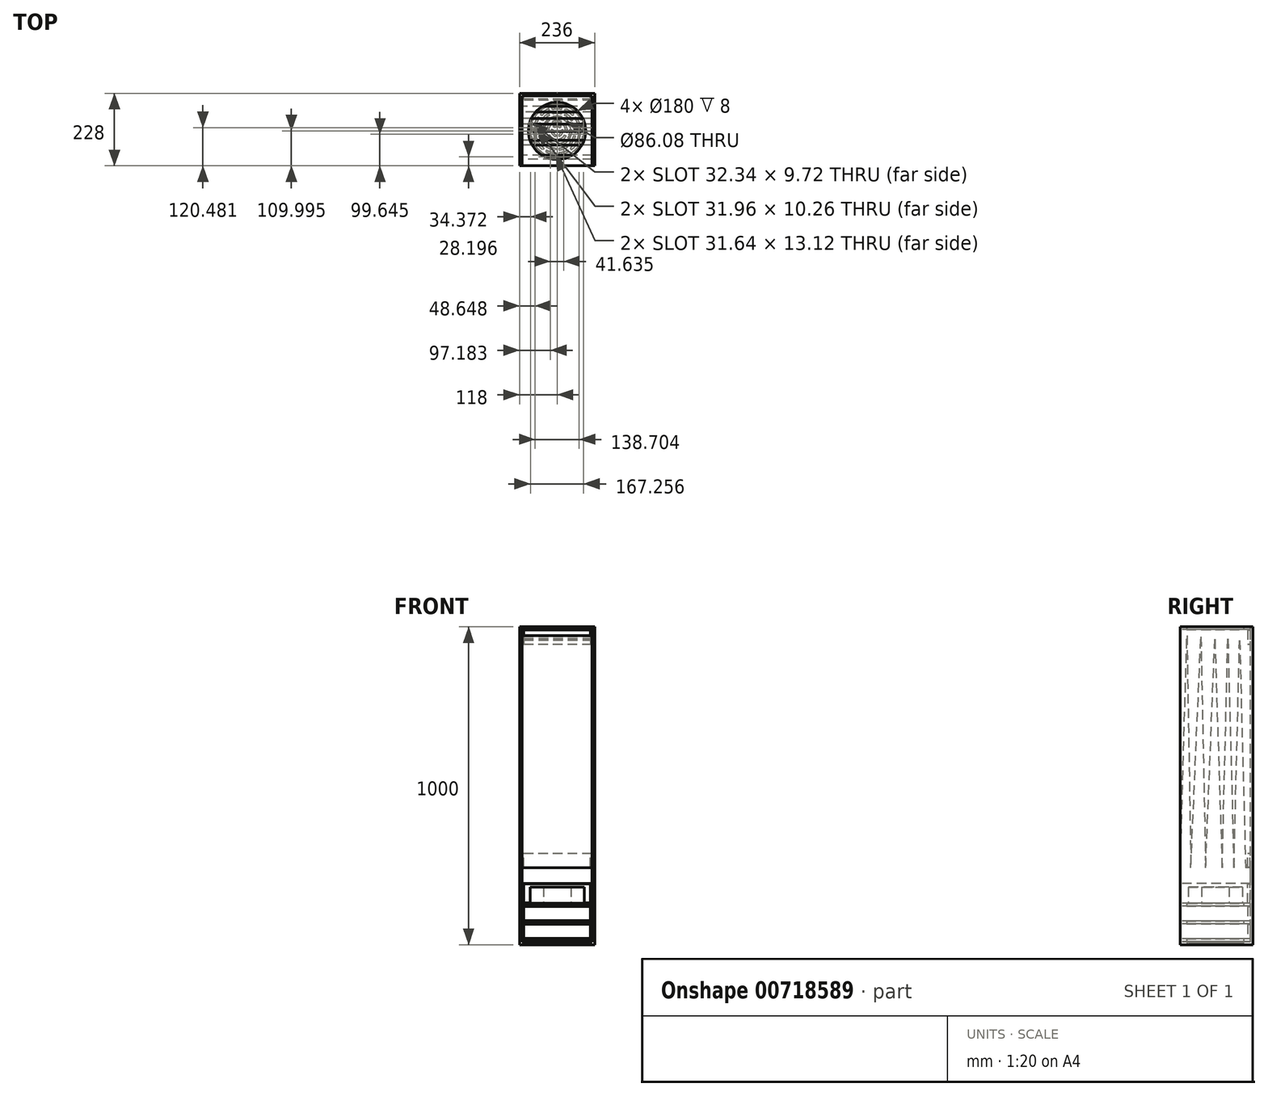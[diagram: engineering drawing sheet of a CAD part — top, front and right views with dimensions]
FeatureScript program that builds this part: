
annotation { "Feature Type Name" : "Feature", "Feature Type Description" : "" }
export const myFeature = defineFeature(function(context is Context, id is Id, definition is map)
    precondition{}
    {
        {
            var Q0;
            Q0=qCreatedBy(makeId("Top.planeOp"),FACE);
            var sketch = newSketch(context, id + "F0", { "sketchPlane" : qUnion([Q0])});
            skCircle(sketch, "E0", {"center": v(5.7, 12.26) * mm, "radius": 90 * mm});
            skLineSegment(sketch, "E1.bottom", {"start": v(-104.3, 122.26) * mm, "end": v(115.7, 122.26) * mm});
            skLineSegment(sketch, "E1.top", {"start": v(-104.3, -97.74) * mm, "end": v(115.7, -97.74) * mm});
            skLineSegment(sketch, "E1.left", {"start": v(-104.3, 122.26) * mm, "end": v(-104.3, -97.74) * mm});
            skLineSegment(sketch, "E1.right", {"start": v(115.7, 122.26) * mm, "end": v(115.7, -97.74) * mm});
            skSolve(sketch);
        }
        {
            var Q0;
            Q0=makeQuery(id+"F0.imprint","IMPRINT",FACE,{"disambiguationData":[TD([[makeQuery(id+"F0.imprint","IMPRINT",EDGE,{"derivedFrom":sQuery(id+"F0.wireOp",EDGE,"E0")}),-1.0]])]});
            extrude(context, id + "F1", {"entities" : qUnion([Q0]), "depth" : 8 * mm, "offsetDistance" : 25 * mm});
        }
        {
            var Q0;
            Q0=makeQuery(id+"F1.opExtrude","SWEPT_FACE",FACE,{"disambiguationData":[OSD([sQuery(id+"F0.wireOp",EDGE,"E1.left")])]});
            var sketch = newSketch(context, id + "F2", { "sketchPlane" : qUnion([Q0])});
            skLineSegment(sketch, "E2.bottom", {"start": v(-122.26, 8) * mm, "end": v(97.74, 8) * mm});
            skLineSegment(sketch, "E2.top", {"start": v(-122.26, -992) * mm, "end": v(97.74, -992) * mm});
            skLineSegment(sketch, "E2.left", {"start": v(-122.26, 8) * mm, "end": v(-122.26, -992) * mm});
            skLineSegment(sketch, "E2.right", {"start": v(97.74, 8) * mm, "end": v(97.74, -992) * mm});
            skSolve(sketch);
        }
        {
            var Q0;
            Q0 = qSketchRegion(id + "F2", true);
            extrude(context, id + "F3", {"entities" : qUnion([Q0]), "depth" : 8 * mm, "offsetDistance" : 25 * mm});
        }
        {
            var Q0;
            Q0=makeQuery(id+"F1.opExtrude","SWEPT_FACE",FACE,{"disambiguationData":[OSD([sQuery(id+"F0.wireOp",EDGE,"E1.bottom")])]});
            var sketch = newSketch(context, id + "F4", { "sketchPlane" : qUnion([Q0])});
            skLineSegment(sketch, "E3.bottom", {"start": v(-123.7, 8) * mm, "end": v(112.3, 8) * mm});
            skLineSegment(sketch, "E3.top", {"start": v(-123.7, -992) * mm, "end": v(112.3, -992) * mm});
            skLineSegment(sketch, "E3.left", {"start": v(-123.7, 8) * mm, "end": v(-123.7, -992) * mm});
            skLineSegment(sketch, "E3.right", {"start": v(112.3, 8) * mm, "end": v(112.3, -992) * mm});
            skSolve(sketch);
        }
        {
            var Q0;
            {var subQ1=sQuery(id+"F0.wireOp",EDGE,"E1.bottom");Q0=makeQuery(id+"F4.imprint","IMPRINT",FACE,{"disambiguationData":[TD([[makeQuery(id+"F4.imprint","IMPRINT",EDGE,{"derivedFrom":makeQuery(id+"F1.opExtrude","CAP_EDGE",EDGE,{"disambiguationData":[OSD([subQ1])],"isStart":true})}),-1.0]])]});}
            var Q1;
            Q1=makeQuery(id+"F4.imprint","IMPRINT",FACE,{"disambiguationData":[TD([[makeQuery(id+"F4.imprint","IMPRINT",EDGE,{"derivedFrom":sQuery(id+"F4.wireOp",EDGE,"E3.top")}),1.0]])]});
            extrude(context, id + "F5", {"entities" : qUnion([Q0, Q1]), "depth" : 8 * mm, "offsetDistance" : 25 * mm});
        }
        {
            var Q0;
            Q0=makeQuery(id+"F3.opExtrude","CAP_FACE",FACE,{"disambiguationData":[OSD([sQuery(id+"F2.wireOp",EDGE,"E2.bottom"),sQuery(id+"F2.wireOp",EDGE,"E2.top"),sQuery(id+"F2.wireOp",EDGE,"E2.left"),sQuery(id+"F2.wireOp",EDGE,"E2.right")])],"isStart":true});
            var sketch = newSketch(context, id + "F6", { "sketchPlane" : qUnion([Q0])});
            skLineSegment(sketch, "E4.top", {"start": v(122.26, -800) * mm, "end": v(-97.74, -800) * mm});
            skLineSegment(sketch, "E4.left", {"start": v(122.26, -750) * mm, "end": v(122.26, -800) * mm});
            skLineSegment(sketch, "E4.right", {"start": v(-97.74, -750) * mm, "end": v(-97.74, -800) * mm});
            skLineSegment(sketch, "E5", {"start": v(-97.74, -750) * mm, "end": v(-76.57, -19.39) * mm});
            skLineSegment(sketch, "E6", {"start": v(-76.57, -19.39) * mm, "end": v(-64.26, -750) * mm});
            skLineSegment(sketch, "E7", {"start": v(-64.26, -750) * mm, "end": v(-32.8, -23.5) * mm});
            skLineSegment(sketch, "E8", {"start": v(-32.8, -23.5) * mm, "end": v(-17.75, -750) * mm});
            skLineSegment(sketch, "E9", {"start": v(-17.75, -750) * mm, "end": v(10.98, -31.7) * mm});
            skLineSegment(sketch, "E10", {"start": v(10.98, -31.7) * mm, "end": v(34.23, -750) * mm});
            skLineSegment(sketch, "E11", {"start": v(34.23, -750) * mm, "end": v(52.02, -30.33) * mm});
            skLineSegment(sketch, "E12", {"start": v(52.02, -30.33) * mm, "end": v(71.17, -750) * mm});
            skLineSegment(sketch, "E13", {"start": v(71.17, -750) * mm, "end": v(88.95, -34.44) * mm});
            skLineSegment(sketch, "E14", {"start": v(88.95, -34.44) * mm, "end": v(108, -750) * mm});
            skLineSegment(sketch, "E15", {"start": v(122.26, -750) * mm, "end": v(108, -750) * mm});
            skSolve(sketch);
        }
        {
            var Q0;
            Q0 = qSketchRegion(id + "F6", true);
            extrude(context, id + "F7", {"entities" : qUnion([Q0]), "depth" : 220 * mm, "offsetDistance" : 25 * mm});
        }
        {
            var Q0;
            Q0=makeQuery(id+"F1.opExtrude","SWEPT_BODY",BODY,{"disambiguationData":[OSD([sQuery(id+"F0.wireOp",EDGE,"E0"),sQuery(id+"F0.wireOp",EDGE,"E1.bottom"),sQuery(id+"F0.wireOp",EDGE,"E1.top"),sQuery(id+"F0.wireOp",EDGE,"E1.left"),sQuery(id+"F0.wireOp",EDGE,"E1.right")])]});
            transform(context, id + "F8", {"entities" : qUnion([Q0]), "transformType" : TransformType.TRANSLATION_3D, "dx" : 0 * mm, "dy" : 0 * mm, "dz" : -870 * mm, "makeCopy" : true});
        }
        {
            var Q0;
            Q0=makeQuery(id+"F8.opPattern","COPY",BODY,{"derivedFrom":makeQuery(id+"F1.opExtrude","SWEPT_BODY",BODY,{"disambiguationData":[OSD([sQuery(id+"F0.wireOp",EDGE,"E0"),sQuery(id+"F0.wireOp",EDGE,"E1.bottom"),sQuery(id+"F0.wireOp",EDGE,"E1.top"),sQuery(id+"F0.wireOp",EDGE,"E1.left"),sQuery(id+"F0.wireOp",EDGE,"E1.right")])]}),"instanceName":"1"});
            transform(context, id + "F9", {"entities" : qUnion([Q0]), "transformType" : TransformType.TRANSLATION_3D, "dx" : 0 * mm, "dy" : 0 * mm, "dz" : -122 * mm, "makeCopy" : true});
        }
        {
            var Q0;
            Q0=makeQuery(id+"F8.opPattern","COPY",FACE,{"derivedFrom":makeQuery(id+"F1.opExtrude","CAP_FACE",FACE,{"disambiguationData":[OSD([sQuery(id+"F0.wireOp",EDGE,"E0"),sQuery(id+"F0.wireOp",EDGE,"E1.bottom"),sQuery(id+"F0.wireOp",EDGE,"E1.top"),sQuery(id+"F0.wireOp",EDGE,"E1.left"),sQuery(id+"F0.wireOp",EDGE,"E1.right")])],"isStart":false}),"instanceName":"1"});
            var sketch = newSketch(context, id + "F10", { "sketchPlane" : qUnion([Q0])});
            skCircle(sketch, "E16", {"center": v(5.7, 12.26) * mm, "radius": 85 * mm});
            skCircle(sketch, "E17", {"center": v(5.7, 12.26) * mm, "radius": 43.04 * mm});
            skSolve(sketch);
        }
        {
            var Q0;
            Q0=makeQuery(id+"F10.imprint","IMPRINT",FACE,{"disambiguationData":[TD([[makeQuery(id+"F10.imprint","IMPRINT",EDGE,{"derivedFrom":sQuery(id+"F10.wireOp",EDGE,"E16")}),1.0]])]});
            extrude(context, id + "F11", {"entities" : qUnion([Q0]), "depth" : 51 * mm, "offsetDistance" : 25 * mm});
        }
        {
            var Q0;
            Q0=makeQuery(id+"F9.opPattern","COPY",BODY,{"derivedFrom":makeQuery(id+"F8.opPattern","COPY",BODY,{"derivedFrom":makeQuery(id+"F1.opExtrude","SWEPT_BODY",BODY,{"disambiguationData":[OSD([sQuery(id+"F0.wireOp",EDGE,"E0"),sQuery(id+"F0.wireOp",EDGE,"E1.bottom"),sQuery(id+"F0.wireOp",EDGE,"E1.top"),sQuery(id+"F0.wireOp",EDGE,"E1.left"),sQuery(id+"F0.wireOp",EDGE,"E1.right")])]}),"instanceName":"1"}),"instanceName":"1"});
            transform(context, id + "F12", {"entities" : qUnion([Q0]), "transformType" : TransformType.TRANSLATION_3D, "dx" : 0 * mm, "dy" : 0 * mm, "dz" : 10 * mm, "makeCopy" : true});
        }
        {
            var Q0;
            Q0=makeQuery(id+"F12.opPattern","COPY",BODY,{"derivedFrom":makeQuery(id+"F9.opPattern","COPY",BODY,{"derivedFrom":makeQuery(id+"F8.opPattern","COPY",BODY,{"derivedFrom":makeQuery(id+"F1.opExtrude","SWEPT_BODY",BODY,{"disambiguationData":[OSD([sQuery(id+"F0.wireOp",EDGE,"E0"),sQuery(id+"F0.wireOp",EDGE,"E1.bottom"),sQuery(id+"F0.wireOp",EDGE,"E1.top"),sQuery(id+"F0.wireOp",EDGE,"E1.left"),sQuery(id+"F0.wireOp",EDGE,"E1.right")])]}),"instanceName":"1"}),"instanceName":"1"}),"instanceName":"1"});
            transform(context, id + "F13", {"entities" : qUnion([Q0]), "transformType" : TransformType.TRANSLATION_3D, "dx" : 0 * mm, "dy" : 0 * mm, "dz" : 56 * mm, "makeCopy" : true});
        }
        {
            var Q0;
            Q0=makeQuery(id+"F5.opExtrude","CAP_FACE",FACE,{"disambiguationData":[OSD([sQuery(id+"F4.wireOp",EDGE,"E3.bottom"),sQuery(id+"F4.wireOp",EDGE,"E3.top"),sQuery(id+"F4.wireOp",EDGE,"E3.left"),sQuery(id+"F4.wireOp",EDGE,"E3.right")])],"isStart":true});
            var sketch = newSketch(context, id + "F14", { "sketchPlane" : qUnion([Q0])});
            skLineSegment(sketch, "E18.bottom", {"start": v(-99.3, -928) * mm, "end": v(110.7, -928) * mm});
            skLineSegment(sketch, "E18.top", {"start": v(-99.3, -972) * mm, "end": v(110.7, -972) * mm});
            skLineSegment(sketch, "E18.left", {"start": v(-99.3, -928) * mm, "end": v(-99.3, -972) * mm});
            skLineSegment(sketch, "E18.right", {"start": v(110.7, -928) * mm, "end": v(110.7, -972) * mm});
            skLineSegment(sketch, "E19.bottom", {"start": v(-99.3, -872) * mm, "end": v(110.7, -872) * mm});
            skLineSegment(sketch, "E19.top", {"start": v(-99.3, -916) * mm, "end": v(110.7, -916) * mm});
            skLineSegment(sketch, "E19.left", {"start": v(-99.3, -872) * mm, "end": v(-99.3, -916) * mm});
            skLineSegment(sketch, "E19.right", {"start": v(110.7, -872) * mm, "end": v(110.7, -916) * mm});
            skLineSegment(sketch, "E20.bottom", {"start": v(-99.3, -860) * mm, "end": v(110.7, -860) * mm});
            skLineSegment(sketch, "E20.top", {"start": v(-99.3, -801) * mm, "end": v(110.7, -801) * mm});
            skLineSegment(sketch, "E20.left", {"start": v(-99.3, -860) * mm, "end": v(-99.3, -801) * mm});
            skLineSegment(sketch, "E20.right", {"start": v(110.7, -860) * mm, "end": v(110.7, -801) * mm});
            skLineSegment(sketch, "E21.bottom", {"start": v(-99.3, -748) * mm, "end": v(110.7, -748) * mm});
            skLineSegment(sketch, "E21.top", {"start": v(-99.3, -704) * mm, "end": v(110.7, -704) * mm});
            skLineSegment(sketch, "E21.left", {"start": v(-99.3, -748) * mm, "end": v(-99.3, -704) * mm});
            skLineSegment(sketch, "E21.right", {"start": v(110.7, -748) * mm, "end": v(110.7, -704) * mm});
            skLineSegment(sketch, "E22.bottom", {"start": v(-99.3, -2) * mm, "end": v(110.7, -2) * mm});
            skLineSegment(sketch, "E22.top", {"start": v(-99.3, -46) * mm, "end": v(110.7, -46) * mm});
            skLineSegment(sketch, "E22.left", {"start": v(-99.3, -2) * mm, "end": v(-99.3, -46) * mm});
            skLineSegment(sketch, "E22.right", {"start": v(110.7, -2) * mm, "end": v(110.7, -46) * mm});
            skSolve(sketch);
        }
        {
            var Q0;
            Q0 = qSketchRegion(id + "F14", true);
            extrude(context, id + "F15", {"entities" : qUnion([Q0]), "depth" : 8 * mm, "offsetDistance" : 25 * mm});
        }
        {
            var Q0;
            Q0=makeQuery(id+"F3.opExtrude","SWEPT_BODY",BODY,{"disambiguationData":[OSD([sQuery(id+"F2.wireOp",EDGE,"E2.bottom"),sQuery(id+"F2.wireOp",EDGE,"E2.top"),sQuery(id+"F2.wireOp",EDGE,"E2.left"),sQuery(id+"F2.wireOp",EDGE,"E2.right")])]});
            transform(context, id + "F16", {"entities" : qUnion([Q0]), "transformType" : TransformType.TRANSLATION_3D, "dx" : 228 * mm, "dy" : 0 * mm, "dz" : 0 * mm, "makeCopy" : true});
        }
        {
            var Q0;
            Q0=makeQuery(id+"F9.opPattern","COPY",FACE,{"derivedFrom":makeQuery(id+"F8.opPattern","COPY",FACE,{"derivedFrom":makeQuery(id+"F1.opExtrude","CAP_FACE",FACE,{"disambiguationData":[OSD([sQuery(id+"F0.wireOp",EDGE,"E0"),sQuery(id+"F0.wireOp",EDGE,"E1.bottom"),sQuery(id+"F0.wireOp",EDGE,"E1.top"),sQuery(id+"F0.wireOp",EDGE,"E1.left"),sQuery(id+"F0.wireOp",EDGE,"E1.right")])],"isStart":true}),"instanceName":"1"}),"instanceName":"1"});
            var sketch = newSketch(context, id + "F17", { "sketchPlane" : qUnion([Q0])});
            skArc(sketch, "E23", {"start": v(18.11, -13.65) * mm, "mid": v(16.52, -6) * mm, "end": v(10.7, -0.8) * mm});
            skArc(sketch, "E24", {"start": v(23.62, -16.83) * mm, "mid": v(21.71, -3) * mm, "end": v(10.7, 5.56) * mm});
            skArc(sketch, "E25.0", {"start": v(-20.6, -8.97) * mm, "mid": v(-19.51, -20.44) * mm, "end": v(-13.65, -30.37) * mm});
            skArc(sketch, "E26.0", {"start": v(-26.4, -7.09) * mm, "mid": v(-25.22, -22.3) * mm, "end": v(-17.23, -35.3) * mm});
            skArc(sketch, "E27.0", {"start": v(-28.85, 8.9) * mm, "mid": v(-33.8, -3.24) * mm, "end": v(-34.6, -16.32) * mm});
            skArc(sketch, "E28.0", {"start": v(-33.57, 12.66) * mm, "mid": v(-39.64, -1.9) * mm, "end": v(-40.5, -17.67) * mm});
            skArc(sketch, "E29.0", {"start": v(-48.62, -7.76) * mm, "mid": v(-47.98, -21.72) * mm, "end": v(-43.8, -35.06) * mm});
            skArc(sketch, "E30.0", {"start": v(-54.56, -6.7) * mm, "mid": v(-53.9, -22.76) * mm, "end": v(-49.03, -38.07) * mm});
            skArc(sketch, "E31.0", {"start": v(-8.76, -79.21) * mm, "mid": v(5.7, -80.76) * mm, "end": v(20.14, -79.21) * mm});
            skArc(sketch, "E32.0", {"start": v(-10.45, -84.99) * mm, "mid": v(5.7, -86.76) * mm, "end": v(21.83, -84.99) * mm});
            skArc(sketch, "E33.0", {"start": v(-9.16, -93.4) * mm, "mid": v(5.7, -94.76) * mm, "end": v(20.54, -93.4) * mm});
            skArc(sketch, "E34.0", {"start": v(-10.6, -99.24) * mm, "mid": v(5.7, -100.76) * mm, "end": v(21.98, -99.24) * mm});
            skLineSegment(sketch, "E35.0", {"start": v(0.7, -0.8) * mm, "end": v(0.7, 5.56) * mm});
            skLineSegment(sketch, "E36.0", {"start": v(10.7, -0.8) * mm, "end": v(10.7, 5.56) * mm});
            skLineSegment(sketch, "E37.trimOffspring", {"start": v(0.7, 13.77) * mm, "end": v(0.7, 19.86) * mm});
            skLineSegment(sketch, "E38.trimOffspring", {"start": v(10.7, 13.77) * mm, "end": v(10.7, 19.86) * mm});
            skLineSegment(sketch, "E39.trimOffspring", {"start": v(10.7, 27.93) * mm, "end": v(10.7, 33.97) * mm});
            skLineSegment(sketch, "E40.trimOffspring", {"start": v(0.7, 27.93) * mm, "end": v(0.7, 33.97) * mm});
            skLineSegment(sketch, "E41.trimOffspring", {"start": v(10.7, 42.01) * mm, "end": v(10.7, 48.04) * mm});
            skLineSegment(sketch, "E42.trimOffspring", {"start": v(0.7, 42.01) * mm, "end": v(0.7, 48.04) * mm});
            skLineSegment(sketch, "E43.trimOffspring", {"start": v(0.7, 56.06) * mm, "end": v(0.7, 62.08) * mm});
            skLineSegment(sketch, "E44.trimOffspring", {"start": v(10.7, 56.06) * mm, "end": v(10.7, 62.08) * mm});
            skLineSegment(sketch, "E45.trimOffspring", {"start": v(10.7, 70.1) * mm, "end": v(10.7, 76.1) * mm});
            skLineSegment(sketch, "E46.trimOffspring", {"start": v(0.7, 70.1) * mm, "end": v(0.7, 76.1) * mm});
            skLineSegment(sketch, "E47.1.0", {"start": v(-6.73, -13.65) * mm, "end": v(-12.24, -16.83) * mm});
            skLineSegment(sketch, "E47.1.1", {"start": v(-1.73, -22.31) * mm, "end": v(-7.24, -25.5) * mm});
            skLineSegment(sketch, "E47.2.0", {"start": v(13.11, -22.31) * mm, "end": v(18.62, -25.5) * mm});
            skLineSegment(sketch, "E47.2.1", {"start": v(18.11, -13.65) * mm, "end": v(23.62, -16.83) * mm});
            skLineSegment(sketch, "E48.1.0", {"start": v(-17.52, 0.54) * mm, "end": v(-23.3, 2.42) * mm});
            skLineSegment(sketch, "E48.1.1", {"start": v(-20.6, -8.97) * mm, "end": v(-26.4, -7.09) * mm});
            skLineSegment(sketch, "E48.2.0", {"start": v(-13.65, -30.37) * mm, "end": v(-17.23, -35.3) * mm});
            skLineSegment(sketch, "E48.2.1", {"start": v(-5.56, -36.25) * mm, "end": v(-9.14, -41.17) * mm});
            skLineSegment(sketch, "E48.3.0", {"start": v(16.94, -36.25) * mm, "end": v(20.52, -41.17) * mm});
            skLineSegment(sketch, "E48.3.1", {"start": v(25.03, -30.37) * mm, "end": v(28.61, -35.3) * mm});
            skLineSegment(sketch, "E48.4.0", {"start": v(31.99, -8.97) * mm, "end": v(37.78, -7.09) * mm});
            skLineSegment(sketch, "E48.4.1", {"start": v(28.9, 0.54) * mm, "end": v(34.69, 2.42) * mm});
            skLineSegment(sketch, "E49.1.0", {"start": v(-22.61, 16.71) * mm, "end": v(-27.34, 20.48) * mm});
            skLineSegment(sketch, "E49.1.1", {"start": v(-28.85, 8.9) * mm, "end": v(-33.57, 12.66) * mm});
            skLineSegment(sketch, "E49.2.0", {"start": v(-34.6, -16.32) * mm, "end": v(-40.5, -17.67) * mm});
            skLineSegment(sketch, "E49.2.1", {"start": v(-32.38, -26.07) * mm, "end": v(-38.27, -27.42) * mm});
            skLineSegment(sketch, "E49.3.0", {"start": v(-16.25, -46.3) * mm, "end": v(-18.87, -51.74) * mm});
            skLineSegment(sketch, "E49.3.1", {"start": v(-7.24, -50.63) * mm, "end": v(-9.86, -56.08) * mm});
            skLineSegment(sketch, "E49.4.0", {"start": v(18.62, -50.63) * mm, "end": v(21.24, -56.08) * mm});
            skLineSegment(sketch, "E49.4.1", {"start": v(27.63, -46.3) * mm, "end": v(30.25, -51.74) * mm});
            skLineSegment(sketch, "E49.5.0", {"start": v(43.76, -26.07) * mm, "end": v(49.65, -27.42) * mm});
            skLineSegment(sketch, "E49.5.1", {"start": v(45.99, -16.32) * mm, "end": v(51.87, -17.67) * mm});
            skLineSegment(sketch, "E49.6.0", {"start": v(40.23, 8.9) * mm, "end": v(44.95, 12.66) * mm});
            skLineSegment(sketch, "E49.6.1", {"start": v(34, 16.71) * mm, "end": v(38.72, 20.48) * mm});
            skLineSegment(sketch, "E50.1.0", {"start": v(-25.36, 32.53) * mm, "end": v(-29.24, 37.15) * mm});
            skLineSegment(sketch, "E50.1.1", {"start": v(-33.02, 26.1) * mm, "end": v(-36.9, 30.72) * mm});
            skLineSegment(sketch, "E50.2.0", {"start": v(-46.89, 2.1) * mm, "end": v(-52.82, 3.14) * mm});
            skLineSegment(sketch, "E50.2.1", {"start": v(-48.62, -7.76) * mm, "end": v(-54.56, -6.7) * mm});
            skLineSegment(sketch, "E50.3.0", {"start": v(-43.8, -35.06) * mm, "end": v(-49.03, -38.07) * mm});
            skLineSegment(sketch, "E50.3.1", {"start": v(-38.8, -43.72) * mm, "end": v(-44.03, -46.73) * mm});
            skLineSegment(sketch, "E50.4.0", {"start": v(-17.57, -61.54) * mm, "end": v(-19.63, -67.2) * mm});
            skLineSegment(sketch, "E50.4.1", {"start": v(-8.17, -64.96) * mm, "end": v(-10.23, -70.62) * mm});
            skLineSegment(sketch, "E50.5.0", {"start": v(19.55, -64.96) * mm, "end": v(21.61, -70.62) * mm});
            skLineSegment(sketch, "E50.5.1", {"start": v(28.95, -61.54) * mm, "end": v(31.01, -67.2) * mm});
            skLineSegment(sketch, "E50.6.0", {"start": v(50.19, -43.72) * mm, "end": v(55.4, -46.73) * mm});
            skLineSegment(sketch, "E50.6.1", {"start": v(55.19, -35.06) * mm, "end": v(60.4, -38.07) * mm});
            skLineSegment(sketch, "E50.7.0", {"start": v(60, -7.76) * mm, "end": v(65.94, -6.7) * mm});
            skLineSegment(sketch, "E50.7.1", {"start": v(58.27, 2.1) * mm, "end": v(64.2, 3.14) * mm});
            skLineSegment(sketch, "E50.8.0", {"start": v(44.4, 26.1) * mm, "end": v(48.28, 30.72) * mm});
            skLineSegment(sketch, "E50.8.1", {"start": v(36.74, 32.53) * mm, "end": v(40.62, 37.15) * mm});
            skLineSegment(sketch, "E51.1.0", {"start": v(-27.04, 47.92) * mm, "end": v(-30.3, 52.98) * mm});
            skLineSegment(sketch, "E51.1.1", {"start": v(-35.45, 42.51) * mm, "end": v(-38.7, 47.57) * mm});
            skLineSegment(sketch, "E51.2.0", {"start": v(-54.38, 20.67) * mm, "end": v(-59.85, 23.17) * mm});
            skLineSegment(sketch, "E51.2.1", {"start": v(-58.53, 11.58) * mm, "end": v(-64, 14.08) * mm});
            skLineSegment(sketch, "E51.3.0", {"start": v(-62.64, -17.03) * mm, "end": v(-68.6, -17.88) * mm});
            skLineSegment(sketch, "E51.3.1", {"start": v(-61.22, -26.93) * mm, "end": v(-67.17, -27.78) * mm});
            skLineSegment(sketch, "E51.4.0", {"start": v(-49.21, -53.22) * mm, "end": v(-53.76, -57.15) * mm});
            skLineSegment(sketch, "E51.4.1", {"start": v(-42.67, -60.77) * mm, "end": v(-47.21, -64.71) * mm});
            skLineSegment(sketch, "E51.5.0", {"start": v(-18.35, -76.4) * mm, "end": v(-20.05, -82.17) * mm});
            skLineSegment(sketch, "E51.5.1", {"start": v(-8.76, -79.21) * mm, "end": v(-10.45, -84.99) * mm});
            skLineSegment(sketch, "E51.6.0", {"start": v(20.14, -79.21) * mm, "end": v(21.83, -84.99) * mm});
            skLineSegment(sketch, "E51.6.1", {"start": v(29.73, -76.4) * mm, "end": v(31.43, -82.17) * mm});
            skLineSegment(sketch, "E51.7.0", {"start": v(54.05, -60.77) * mm, "end": v(58.6, -64.71) * mm});
            skLineSegment(sketch, "E51.7.1", {"start": v(60.6, -53.22) * mm, "end": v(65.14, -57.15) * mm});
            skLineSegment(sketch, "E51.8.0", {"start": v(72.6, -26.93) * mm, "end": v(78.55, -27.78) * mm});
            skLineSegment(sketch, "E51.8.1", {"start": v(74.02, -17.03) * mm, "end": v(79.98, -17.88) * mm});
            skLineSegment(sketch, "E51.9.0", {"start": v(69.91, 11.58) * mm, "end": v(75.38, 14.08) * mm});
            skLineSegment(sketch, "E51.9.1", {"start": v(65.76, 20.67) * mm, "end": v(71.23, 23.17) * mm});
            skLineSegment(sketch, "E51.10.0", {"start": v(46.83, 42.51) * mm, "end": v(50.08, 47.57) * mm});
            skLineSegment(sketch, "E51.10.1", {"start": v(38.42, 47.92) * mm, "end": v(41.67, 52.98) * mm});
            skLineSegment(sketch, "E52.1.0", {"start": v(-28.15, 62.98) * mm, "end": v(-30.94, 68.3) * mm});
            skLineSegment(sketch, "E52.1.1", {"start": v(-37, 58.34) * mm, "end": v(-39.8, 63.66) * mm});
            skLineSegment(sketch, "E52.2.0", {"start": v(-59.24, 38.64) * mm, "end": v(-64.19, 42.05) * mm});
            skLineSegment(sketch, "E52.2.1", {"start": v(-64.92, 30.4) * mm, "end": v(-69.87, 33.82) * mm});
            skLineSegment(sketch, "E52.3.0", {"start": v(-75.46, 2.63) * mm, "end": v(-81.42, 3.36) * mm});
            skLineSegment(sketch, "E52.3.1", {"start": v(-76.66, -7.3) * mm, "end": v(-82.63, -6.57) * mm});
            skLineSegment(sketch, "E52.4.0", {"start": v(-73.08, -36.78) * mm, "end": v(-78.7, -38.91) * mm});
            skLineSegment(sketch, "E52.4.1", {"start": v(-69.53, -46.13) * mm, "end": v(-75.15, -48.26) * mm});
            skLineSegment(sketch, "E52.5.0", {"start": v(-52.66, -70.58) * mm, "end": v(-56.64, -75.08) * mm});
            skLineSegment(sketch, "E52.5.1", {"start": v(-45.17, -77.2) * mm, "end": v(-49.16, -81.7) * mm});
            skLineSegment(sketch, "E52.6.0", {"start": v(-18.87, -91.01) * mm, "end": v(-20.31, -96.85) * mm});
            skLineSegment(sketch, "E52.6.1", {"start": v(-9.16, -93.4) * mm, "end": v(-10.6, -99.24) * mm});
            skLineSegment(sketch, "E52.7.0", {"start": v(20.54, -93.4) * mm, "end": v(21.98, -99.24) * mm});
            skLineSegment(sketch, "E52.7.1", {"start": v(30.25, -91.01) * mm, "end": v(31.7, -96.85) * mm});
            skLineSegment(sketch, "E52.8.0", {"start": v(56.55, -77.2) * mm, "end": v(60.54, -81.7) * mm});
            skLineSegment(sketch, "E52.8.1", {"start": v(64.04, -70.58) * mm, "end": v(68.03, -75.08) * mm});
            skLineSegment(sketch, "E52.9.0", {"start": v(80.91, -46.13) * mm, "end": v(86.53, -48.26) * mm});
            skLineSegment(sketch, "E52.9.1", {"start": v(84.46, -36.78) * mm, "end": v(90.08, -38.91) * mm});
            skLineSegment(sketch, "E52.10.0", {"start": v(88.04, -7.3) * mm, "end": v(94, -6.57) * mm});
            skLineSegment(sketch, "E52.10.1", {"start": v(86.84, 2.63) * mm, "end": v(92.8, 3.36) * mm});
            skLineSegment(sketch, "E52.11.0", {"start": v(76.3, 30.4) * mm, "end": v(81.25, 33.82) * mm});
            skLineSegment(sketch, "E52.11.1", {"start": v(70.62, 38.64) * mm, "end": v(75.57, 42.05) * mm});
            skLineSegment(sketch, "E52.12.0", {"start": v(48.39, 58.34) * mm, "end": v(51.18, 63.66) * mm});
            skLineSegment(sketch, "E52.12.1", {"start": v(39.53, 62.98) * mm, "end": v(42.33, 68.3) * mm});
            skArc(sketch, "E53.trimOffspring", {"start": v(0.7, -0.8) * mm, "mid": v(-5.14, -6) * mm, "end": v(-6.73, -13.65) * mm});
            skArc(sketch, "E54.trimOffspring", {"start": v(0.7, 5.56) * mm, "mid": v(-10.33, -3) * mm, "end": v(-12.24, -16.83) * mm});
            skArc(sketch, "E55.trimOffspring", {"start": v(-1.73, -22.31) * mm, "mid": v(5.7, -24.76) * mm, "end": v(13.11, -22.31) * mm});
            skArc(sketch, "E56.trimOffspring", {"start": v(-7.24, -25.5) * mm, "mid": v(5.7, -30.76) * mm, "end": v(18.62, -25.5) * mm});
            skArc(sketch, "E57.trimOffspring", {"start": v(0.7, 27.93) * mm, "mid": v(-11.88, 24.23) * mm, "end": v(-22.61, 16.71) * mm});
            skArc(sketch, "E58.trimOffspring", {"start": v(0.7, 33.97) * mm, "mid": v(-14.49, 29.64) * mm, "end": v(-27.34, 20.48) * mm});
            skArc(sketch, "E59.trimOffspring", {"start": v(-5.56, -36.25) * mm, "mid": v(5.7, -38.76) * mm, "end": v(16.94, -36.25) * mm});
            skArc(sketch, "E60.trimOffspring", {"start": v(-9.14, -41.17) * mm, "mid": v(5.7, -44.76) * mm, "end": v(20.52, -41.17) * mm});
            skArc(sketch, "E61.trimOffspring", {"start": v(25.03, -30.37) * mm, "mid": v(30.9, -20.44) * mm, "end": v(31.99, -8.97) * mm});
            skArc(sketch, "E62.trimOffspring", {"start": v(28.61, -35.3) * mm, "mid": v(36.6, -22.3) * mm, "end": v(37.78, -7.09) * mm});
            skArc(sketch, "E63.trimOffspring", {"start": v(28.9, 0.54) * mm, "mid": v(21.27, 9.18) * mm, "end": v(10.7, 13.77) * mm});
            skArc(sketch, "E64.trimOffspring", {"start": v(34.69, 2.42) * mm, "mid": v(24.8, 14.04) * mm, "end": v(10.7, 19.86) * mm});
            skArc(sketch, "E65.trimOffspring", {"start": v(0.7, 13.77) * mm, "mid": v(-9.89, 9.18) * mm, "end": v(-17.52, 0.54) * mm});
            skArc(sketch, "E66.trimOffspring", {"start": v(0.7, 19.86) * mm, "mid": v(-13.41, 14.04) * mm, "end": v(-23.3, 2.42) * mm});
            skArc(sketch, "E67.trimOffspring", {"start": v(34, 16.71) * mm, "mid": v(23.26, 24.23) * mm, "end": v(10.7, 27.93) * mm});
            skArc(sketch, "E68.trimOffspring", {"start": v(38.72, 20.48) * mm, "mid": v(25.87, 29.64) * mm, "end": v(10.7, 33.97) * mm});
            skArc(sketch, "E69.trimOffspring", {"start": v(51.87, -17.67) * mm, "mid": v(51.02, -1.9) * mm, "end": v(44.95, 12.66) * mm});
            skArc(sketch, "E70.trimOffspring", {"start": v(45.99, -16.32) * mm, "mid": v(45.17, -3.24) * mm, "end": v(40.23, 8.9) * mm});
            skArc(sketch, "E71.trimOffspring", {"start": v(27.63, -46.3) * mm, "mid": v(37.35, -37.5) * mm, "end": v(43.76, -26.07) * mm});
            skArc(sketch, "E72.trimOffspring", {"start": v(30.25, -51.74) * mm, "mid": v(42.05, -41.25) * mm, "end": v(49.65, -27.42) * mm});
            skArc(sketch, "E73.trimOffspring", {"start": v(-7.24, -50.63) * mm, "mid": v(5.7, -52.76) * mm, "end": v(18.62, -50.63) * mm});
            skArc(sketch, "E74.trimOffspring", {"start": v(-9.86, -56.08) * mm, "mid": v(5.7, -58.76) * mm, "end": v(21.24, -56.08) * mm});
            skArc(sketch, "E75.trimOffspring", {"start": v(-32.38, -26.07) * mm, "mid": v(-25.97, -37.5) * mm, "end": v(-16.25, -46.3) * mm});
            skArc(sketch, "E76.trimOffspring", {"start": v(-38.27, -27.42) * mm, "mid": v(-30.66, -41.25) * mm, "end": v(-18.87, -51.74) * mm});
            skArc(sketch, "E77.trimOffspring", {"start": v(-36.9, 30.72) * mm, "mid": v(-46.7, 18) * mm, "end": v(-52.82, 3.14) * mm});
            skArc(sketch, "E78.trimOffspring", {"start": v(-33.02, 26.1) * mm, "mid": v(-41.5, 15) * mm, "end": v(-46.89, 2.1) * mm});
            skArc(sketch, "E79.trimOffspring", {"start": v(0.7, 42.01) * mm, "mid": v(-12.95, 38.96) * mm, "end": v(-25.36, 32.53) * mm});
            skArc(sketch, "E80.trimOffspring", {"start": v(0.7, 48.04) * mm, "mid": v(-15, 44.6) * mm, "end": v(-29.24, 37.15) * mm});
            skArc(sketch, "E81.trimOffspring", {"start": v(40.62, 37.15) * mm, "mid": v(26.38, 44.6) * mm, "end": v(10.7, 48.04) * mm});
            skArc(sketch, "E82.trimOffspring", {"start": v(36.74, 32.53) * mm, "mid": v(24.33, 38.96) * mm, "end": v(10.7, 42.01) * mm});
            skArc(sketch, "E83.trimOffspring", {"start": v(58.27, 2.1) * mm, "mid": v(52.89, 15) * mm, "end": v(44.4, 26.1) * mm});
            skArc(sketch, "E84.trimOffspring", {"start": v(64.2, 3.14) * mm, "mid": v(58.08, 18) * mm, "end": v(48.28, 30.72) * mm});
            skArc(sketch, "E85.trimOffspring", {"start": v(60.4, -38.07) * mm, "mid": v(65.27, -22.76) * mm, "end": v(65.94, -6.7) * mm});
            skArc(sketch, "E86.trimOffspring", {"start": v(55.19, -35.06) * mm, "mid": v(59.36, -21.72) * mm, "end": v(60, -7.76) * mm});
            skArc(sketch, "E87.trimOffspring", {"start": v(28.95, -61.54) * mm, "mid": v(40.72, -54) * mm, "end": v(50.19, -43.72) * mm});
            skArc(sketch, "E88.trimOffspring", {"start": v(31.01, -67.2) * mm, "mid": v(44.58, -58.6) * mm, "end": v(55.4, -46.73) * mm});
            skArc(sketch, "E89.trimOffspring", {"start": v(-8.17, -64.96) * mm, "mid": v(5.7, -66.76) * mm, "end": v(19.55, -64.96) * mm});
            skArc(sketch, "E90.trimOffspring", {"start": v(-10.23, -70.62) * mm, "mid": v(5.7, -72.76) * mm, "end": v(21.61, -70.62) * mm});
            skArc(sketch, "E91.trimOffspring", {"start": v(-44.03, -46.73) * mm, "mid": v(-33.2, -58.6) * mm, "end": v(-19.63, -67.2) * mm});
            skArc(sketch, "E92.trimOffspring", {"start": v(-38.8, -43.72) * mm, "mid": v(-29.34, -54) * mm, "end": v(-17.57, -61.54) * mm});
            skArc(sketch, "E93.trimOffspring", {"start": v(-42.67, -60.77) * mm, "mid": v(-31.34, -69.88) * mm, "end": v(-18.35, -76.4) * mm});
            skArc(sketch, "E94.trimOffspring", {"start": v(-45.17, -77.2) * mm, "mid": v(-32.65, -85.3) * mm, "end": v(-18.87, -91.01) * mm});
            skArc(sketch, "E95.trimOffspring", {"start": v(-49.16, -81.7) * mm, "mid": v(-35.44, -90.62) * mm, "end": v(-20.31, -96.85) * mm});
            skArc(sketch, "E96.trimOffspring", {"start": v(-75.15, -48.26) * mm, "mid": v(-67.14, -62.53) * mm, "end": v(-56.64, -75.08) * mm});
            skArc(sketch, "E97.trimOffspring", {"start": v(-69.53, -46.13) * mm, "mid": v(-62.2, -59.12) * mm, "end": v(-52.66, -70.58) * mm});
            skArc(sketch, "E98.trimOffspring", {"start": v(-67.17, -27.78) * mm, "mid": v(-50.61, -61.04) * mm, "end": v(-20.05, -82.17) * mm});
            skArc(sketch, "E99.trimOffspring", {"start": v(-61.22, -26.93) * mm, "mid": v(-56.62, -40.71) * mm, "end": v(-49.21, -53.22) * mm});
            skArc(sketch, "E100.trimOffspring", {"start": v(-76.66, -7.3) * mm, "mid": v(-76.2, -22.2) * mm, "end": v(-73.08, -36.78) * mm});
            skArc(sketch, "E101.trimOffspring", {"start": v(-82.63, -6.57) * mm, "mid": v(-82.16, -22.92) * mm, "end": v(-78.7, -38.91) * mm});
            skArc(sketch, "E102.trimOffspring", {"start": v(-64.92, 30.4) * mm, "mid": v(-71.45, 17) * mm, "end": v(-75.46, 2.63) * mm});
            skArc(sketch, "E103.trimOffspring", {"start": v(-58.53, 11.58) * mm, "mid": v(-62.11, -2.5) * mm, "end": v(-62.64, -17.03) * mm});
            skArc(sketch, "E104.trimOffspring", {"start": v(-64, 14.08) * mm, "mid": v(-68.05, -1.65) * mm, "end": v(-68.6, -17.88) * mm});
            skArc(sketch, "E105.trimOffspring", {"start": v(-69.87, 33.82) * mm, "mid": v(-77.06, 19.13) * mm, "end": v(-81.42, 3.36) * mm});
            skArc(sketch, "E106.trimOffspring", {"start": v(-38.7, 47.57) * mm, "mid": v(-50.61, 36.53) * mm, "end": v(-59.85, 23.17) * mm});
            skArc(sketch, "E107.trimOffspring", {"start": v(-35.45, 42.51) * mm, "mid": v(-46.08, 32.6) * mm, "end": v(-54.38, 20.67) * mm});
            skArc(sketch, "E108.trimOffspring", {"start": v(-39.8, 63.66) * mm, "mid": v(-53, 53.99) * mm, "end": v(-64.19, 42.05) * mm});
            skArc(sketch, "E109.trimOffspring", {"start": v(-37, 58.34) * mm, "mid": v(-49.02, 49.5) * mm, "end": v(-59.24, 38.64) * mm});
            skArc(sketch, "E110.trimOffspring", {"start": v(0.7, 70.1) * mm, "mid": v(-14.05, 67.85) * mm, "end": v(-28.15, 62.98) * mm});
            skArc(sketch, "E111.trimOffspring", {"start": v(0.7, 76.1) * mm, "mid": v(-15.49, 73.67) * mm, "end": v(-30.94, 68.3) * mm});
            skArc(sketch, "E112.trimOffspring", {"start": v(42.33, 68.3) * mm, "mid": v(26.87, 73.67) * mm, "end": v(10.7, 76.1) * mm});
            skArc(sketch, "E113.trimOffspring", {"start": v(39.53, 62.98) * mm, "mid": v(25.43, 67.85) * mm, "end": v(10.7, 70.1) * mm});
            skArc(sketch, "E114.trimOffspring", {"start": v(0.7, 62.08) * mm, "mid": v(-15.3, 59.23) * mm, "end": v(-30.3, 52.98) * mm});
            skArc(sketch, "E115.trimOffspring", {"start": v(0.7, 56.06) * mm, "mid": v(-13.6, 53.47) * mm, "end": v(-27.04, 47.92) * mm});
            skArc(sketch, "E116.trimOffspring", {"start": v(38.42, 47.92) * mm, "mid": v(24.99, 53.47) * mm, "end": v(10.7, 56.06) * mm});
            skArc(sketch, "E117.trimOffspring", {"start": v(41.67, 52.98) * mm, "mid": v(26.68, 59.23) * mm, "end": v(10.7, 62.08) * mm});
            skArc(sketch, "E118.trimOffspring", {"start": v(75.57, 42.05) * mm, "mid": v(64.38, 53.99) * mm, "end": v(51.18, 63.66) * mm});
            skArc(sketch, "E119.trimOffspring", {"start": v(70.62, 38.64) * mm, "mid": v(60.4, 49.5) * mm, "end": v(48.39, 58.34) * mm});
            skArc(sketch, "E120.trimOffspring", {"start": v(71.23, 23.17) * mm, "mid": v(62, 36.53) * mm, "end": v(50.08, 47.57) * mm});
            skArc(sketch, "E121.trimOffspring", {"start": v(92.8, 3.36) * mm, "mid": v(88.44, 19.13) * mm, "end": v(81.25, 33.82) * mm});
            skArc(sketch, "E122.trimOffspring", {"start": v(65.76, 20.67) * mm, "mid": v(57.46, 32.6) * mm, "end": v(46.83, 42.51) * mm});
            skArc(sketch, "E123.trimOffspring", {"start": v(86.84, 2.63) * mm, "mid": v(82.83, 17) * mm, "end": v(76.3, 30.4) * mm});
            skArc(sketch, "E124.trimOffspring", {"start": v(90.08, -38.91) * mm, "mid": v(93.54, -22.92) * mm, "end": v(94, -6.57) * mm});
            skArc(sketch, "E125.trimOffspring", {"start": v(74.02, -17.03) * mm, "mid": v(73.5, -2.5) * mm, "end": v(69.91, 11.58) * mm});
            skArc(sketch, "E126.trimOffspring", {"start": v(84.46, -36.78) * mm, "mid": v(87.59, -22.2) * mm, "end": v(88.04, -7.3) * mm});
            skArc(sketch, "E127.trimOffspring", {"start": v(79.98, -17.88) * mm, "mid": v(79.43, -1.65) * mm, "end": v(75.38, 14.08) * mm});
            skArc(sketch, "E128.trimOffspring", {"start": v(60.6, -53.22) * mm, "mid": v(68, -40.71) * mm, "end": v(72.6, -26.93) * mm});
            skArc(sketch, "E129.trimOffspring", {"start": v(65.14, -57.15) * mm, "mid": v(73.46, -43.2) * mm, "end": v(78.55, -27.78) * mm});
            skArc(sketch, "E130.trimOffspring", {"start": v(64.04, -70.58) * mm, "mid": v(73.59, -59.12) * mm, "end": v(80.91, -46.13) * mm});
            skArc(sketch, "E131.trimOffspring", {"start": v(29.73, -76.4) * mm, "mid": v(42.72, -69.88) * mm, "end": v(54.05, -60.77) * mm});
            skArc(sketch, "E132.trimOffspring", {"start": v(68.03, -75.08) * mm, "mid": v(78.52, -62.53) * mm, "end": v(86.53, -48.26) * mm});
            skArc(sketch, "E133.trimOffspring", {"start": v(31.43, -82.17) * mm, "mid": v(45.97, -74.93) * mm, "end": v(58.6, -64.71) * mm});
            skArc(sketch, "E134.trimOffspring", {"start": v(31.7, -96.85) * mm, "mid": v(46.82, -90.62) * mm, "end": v(60.54, -81.7) * mm});
            skArc(sketch, "E135.trimOffspring", {"start": v(30.25, -91.01) * mm, "mid": v(44.03, -85.3) * mm, "end": v(56.55, -77.2) * mm});
            skSolve(sketch);
        }
        {
            var Q0;
            Q0 = qSketchRegion(id + "Fh9oX6n1rAjzbkG_10", true);
            var Q1;
            Q1=makeQuery(id+"F17.imprint","IMPRINT",FACE,{"disambiguationData":[TD([[makeQuery(id+"F17.imprint","IMPRINT",EDGE,{"derivedFrom":makeQuery(id+"F9.opPattern","COPY",EDGE,{"derivedFrom":makeQuery(id+"F8.opPattern","COPY",EDGE,{"derivedFrom":makeQuery(id+"F1.opExtrude","CAP_EDGE",EDGE,{"disambiguationData":[OSD([sQuery(id+"F0.wireOp",EDGE,"E0")])],"isStart":true}),"instanceName":"1"}),"instanceName":"1"})}),1.0]])]});
            var Q2;
            Q2=makeQuery(id+"F17.imprint","IMPRINT",FACE,{"disambiguationData":[TD([[makeQuery(id+"F17.imprint","IMPRINT",EDGE,{"derivedFrom":sQuery(id+"F17.wireOp",EDGE,"E23")}),1.0]])]});
            extrude(context, id + "F18", {"entities" : qUnion([Q0, Q1, Q2]), "operationType" : NewBodyOperationType.ADD, "oppositeDirection" : true, "depth" : 8 * mm, "offsetDistance" : 25 * mm});
        }
    });
